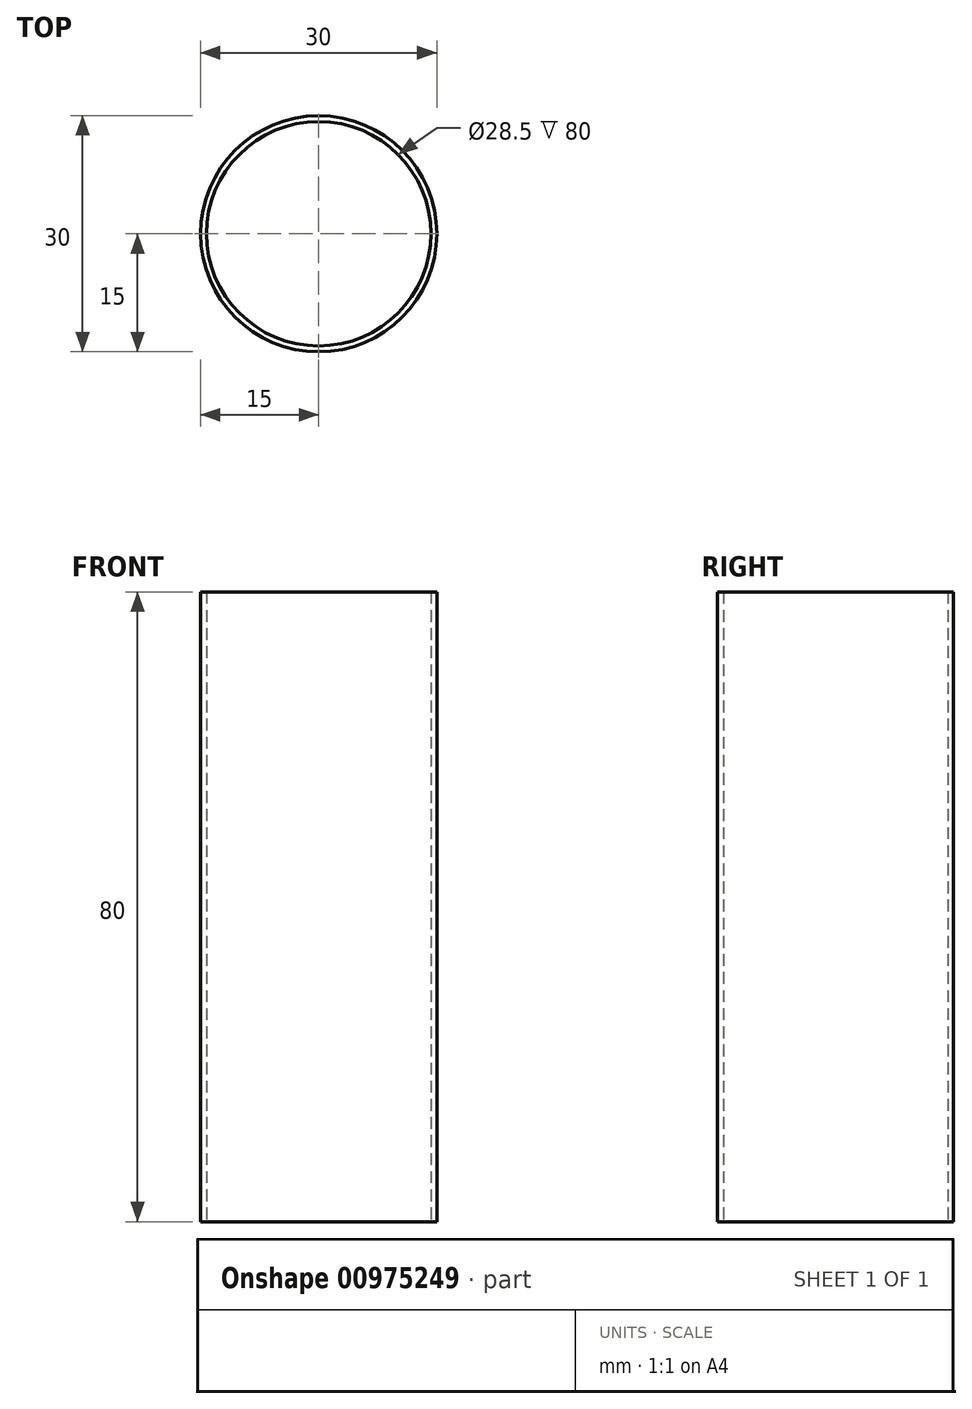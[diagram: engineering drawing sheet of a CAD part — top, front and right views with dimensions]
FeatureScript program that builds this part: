
annotation { "Feature Type Name" : "Feature", "Feature Type Description" : "" }
export const myFeature = defineFeature(function(context is Context, id is Id, definition is map)
    precondition{}
    {
        {
            var Q0;
            Q0=qCreatedBy(makeId("Top.planeOp"),FACE);
            var sketch = newSketch(context, id + "F0", { "sketchPlane" : qUnion([Q0])});
            skCircle(sketch, "E0", {"center": v(0, 0) * mm, "radius": 14.25 * mm});
            skCircle(sketch, "E1", {"center": v(0, 0) * mm, "radius": 15 * mm});
            skSolve(sketch);
        }
        {
            var Q0;
            Q0=makeQuery(id+"F0.imprint","IMPRINT",FACE,{"disambiguationData":[TD([[makeQuery(id+"F0.imprint","IMPRINT",EDGE,{"derivedFrom":sQuery(id+"F0.wireOp",EDGE,"E0")}),-1.0]])]});
            extrude(context, id + "F1", {"entities" : qUnion([Q0]), "depth" : 80 * mm, "offsetDistance" : 25 * mm});
        }
    });
